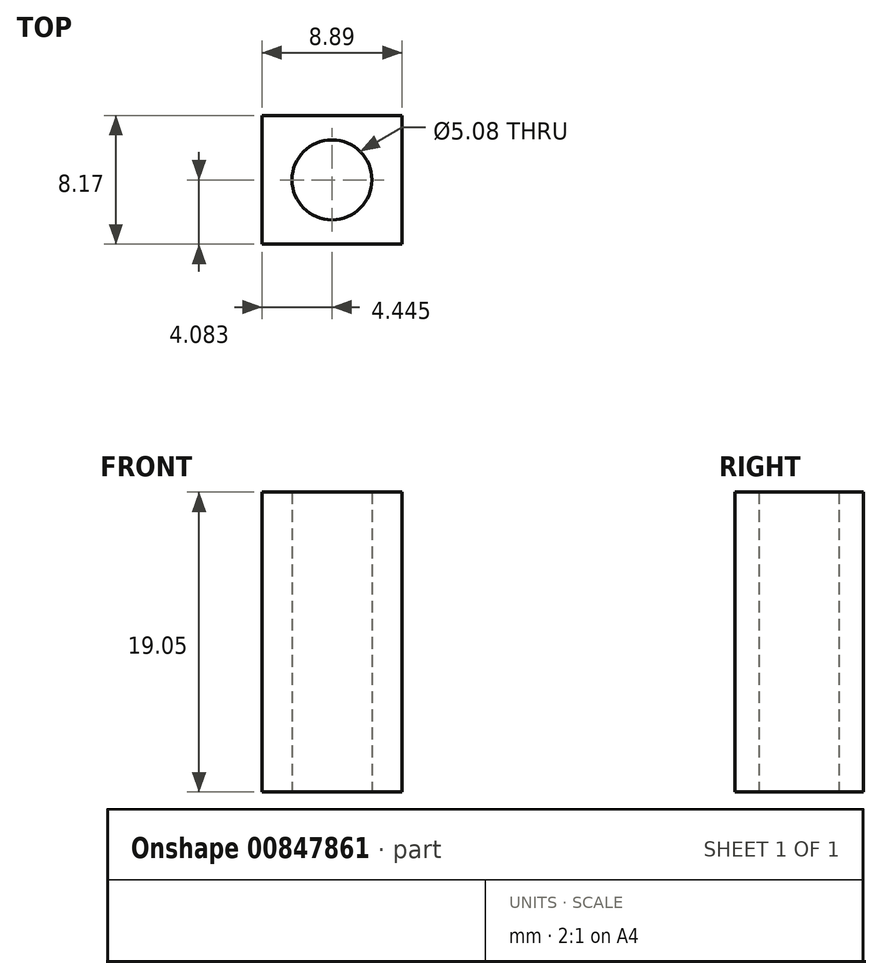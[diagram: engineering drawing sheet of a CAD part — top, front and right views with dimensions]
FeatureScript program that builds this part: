
annotation { "Feature Type Name" : "Feature", "Feature Type Description" : "" }
export const myFeature = defineFeature(function(context is Context, id is Id, definition is map)
    precondition{}
    {
        {
            var Q0;
            Q0=qCreatedBy(makeId("Top.planeOp"),FACE);
            var sketch = newSketch(context, id + "F0", { "sketchPlane" : qUnion([Q0])});
            skLineSegment(sketch, "E0.bottom", {"start": v(0, 0) * mm, "end": v(8.9, 0) * mm});
            skLineSegment(sketch, "E0.top", {"start": v(0, 8.17) * mm, "end": v(8.89, 8.17) * mm});
            skLineSegment(sketch, "E0.left", {"start": v(0, 0) * mm, "end": v(0, 8.17) * mm});
            skLineSegment(sketch, "E0.right", {"start": v(8.9, 0) * mm, "end": v(8.89, 8.17) * mm});
            skCircle(sketch, "E1", {"center": v(4.45, 4.08) * mm, "radius": 2.54 * mm});
            skSolve(sketch);
        }
        {
            var Q0;
            Q0 = qSketchRegion(id + "F0", true);
            extrude(context, id + "F1", {"entities" : qUnion([Q0]), "depth" : 19.05 * mm, "offsetDistance" : 25.4 * mm});
        }
    });
